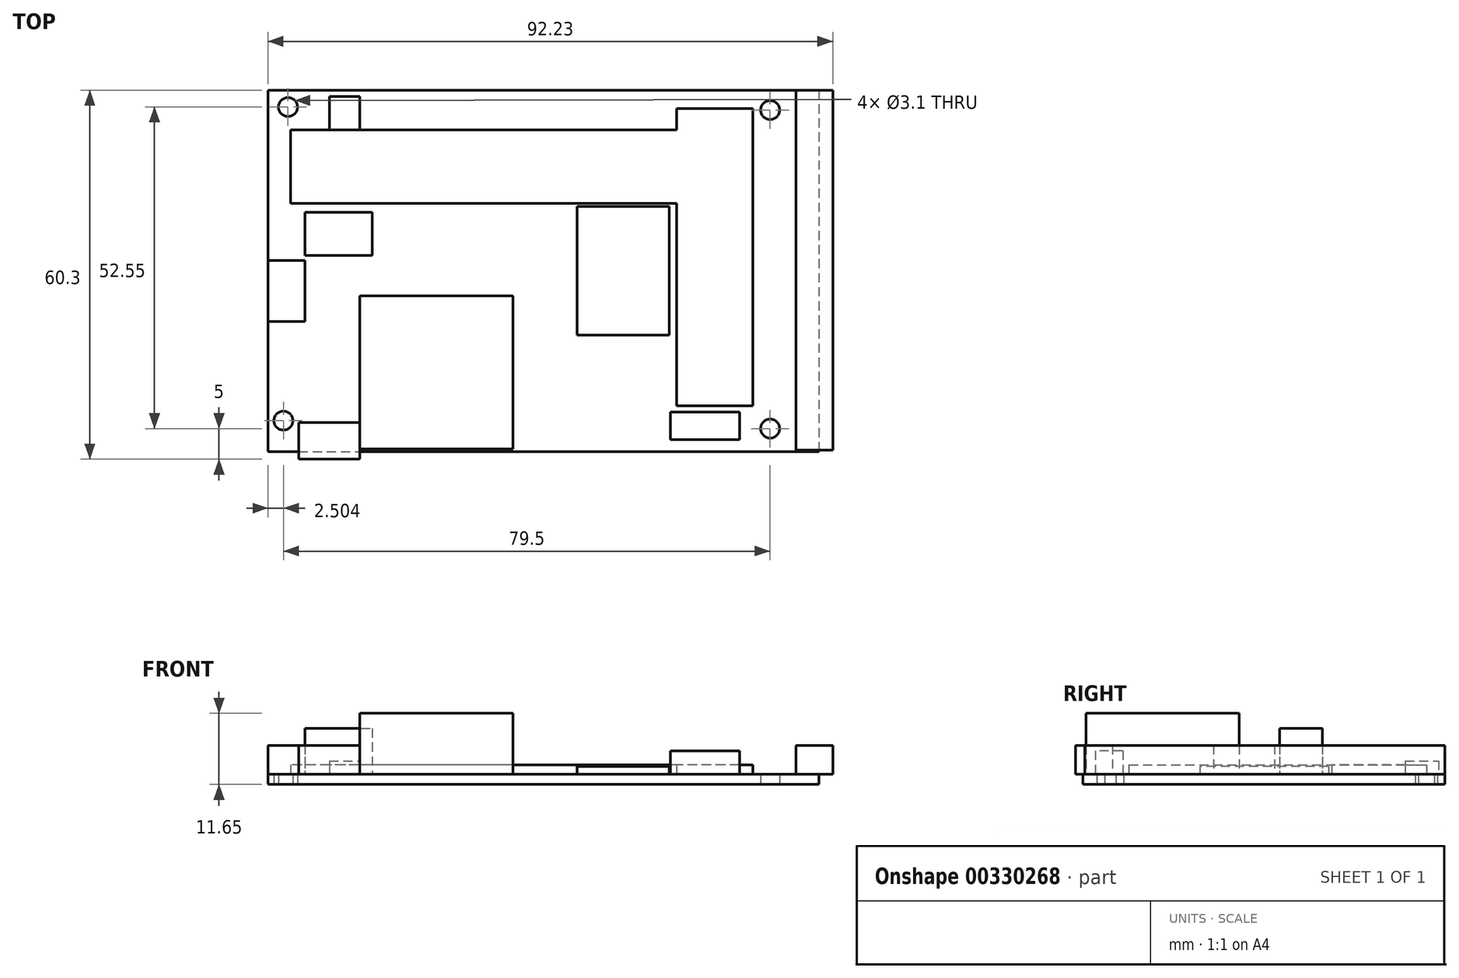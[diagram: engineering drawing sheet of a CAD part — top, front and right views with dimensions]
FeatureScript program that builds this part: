
annotation { "Feature Type Name" : "Feature", "Feature Type Description" : "" }
export const myFeature = defineFeature(function(context is Context, id is Id, definition is map)
    precondition{}
    {
        {
            var Q0;
            Q0=qCreatedBy(makeId("Top.planeOp"),FACE);
            var sketch = newSketch(context, id + "F0", { "sketchPlane" : qUnion([Q0])});
            skLineSegment(sketch, "E0.bottom", {"start": v(-45.78, 29.32) * mm, "end": v(44.22, 29.32) * mm});
            skLineSegment(sketch, "E0.top", {"start": v(-45.78, -29.78) * mm, "end": v(44.22, -29.78) * mm});
            skLineSegment(sketch, "E0.left", {"start": v(-45.78, 29.32) * mm, "end": v(-45.78, -29.78) * mm});
            skLineSegment(sketch, "E0.right", {"start": v(44.22, 29.32) * mm, "end": v(44.22, -29.78) * mm});
            skCircle(sketch, "E1", {"center": v(-43.28, -24.68) * mm, "radius": 1.55 * mm});
            skCircle(sketch, "E2", {"center": v(-42.53, 26.57) * mm, "radius": 1.55 * mm});
            skCircle(sketch, "E3", {"center": v(36.22, 26.07) * mm, "radius": 1.55 * mm});
            skCircle(sketch, "E4", {"center": v(36.22, -25.98) * mm, "radius": 1.55 * mm});
            skSolve(sketch);
        }
        {
            var Q0;
            Q0=makeQuery(id+"F0.imprint","IMPRINT",FACE,{"disambiguationData":[TD([[makeQuery(id+"F0.imprint","IMPRINT",EDGE,{"derivedFrom":sQuery(id+"F0.wireOp",EDGE,"E0.bottom")}),-1.0]])]});
            extrude(context, id + "F1", {"entities" : qUnion([Q0]), "depth" : 1.65 * mm});
        }
        {
            var Q0;
            Q0=qCreatedBy(makeId("Top.planeOp"),FACE);
            var sketch = newSketch(context, id + "F2", { "sketchPlane" : qUnion([Q0])});
            skLineSegment(sketch, "E5.bottom", {"start": v(33.42, -22.28) * mm, "end": v(20.92, -22.28) * mm});
            skLineSegment(sketch, "E5.top", {"start": v(33.42, 26.32) * mm, "end": v(20.92, 26.32) * mm});
            skLineSegment(sketch, "E5.left", {"start": v(33.42, -22.28) * mm, "end": v(33.42, 26.32) * mm});
            skLineSegment(sketch, "E5.right", {"start": v(20.92, -22.28) * mm, "end": v(20.92, 26.32) * mm});
            skLineSegment(sketch, "E6.bottom", {"start": v(20.92, 22.82) * mm, "end": v(-42.08, 22.82) * mm});
            skLineSegment(sketch, "E6.top", {"start": v(20.92, 10.82) * mm, "end": v(-42.08, 10.82) * mm});
            skLineSegment(sketch, "E6.left", {"start": v(20.92, 22.82) * mm, "end": v(20.92, 10.82) * mm});
            skLineSegment(sketch, "E6.right", {"start": v(-42.08, 22.82) * mm, "end": v(-42.08, 10.82) * mm});
            skSolve(sketch);
        }
        {
            var Q0;
            Q0 = qSketchRegion(id + "F2", true);
            extrude(context, id + "F3", {"entities" : qUnion([Q0]), "operationType" : NewBodyOperationType.ADD, "depth" : 3.2 * mm});
        }
        {
            var Q0;
            Q0=makeQuery(id+"F1.opExtrude","CAP_FACE",FACE,{"disambiguationData":[OSD([sQuery(id+"F0.wireOp",EDGE,"E0.bottom"),sQuery(id+"F0.wireOp",EDGE,"E0.top"),sQuery(id+"F0.wireOp",EDGE,"E0.left"),sQuery(id+"F0.wireOp",EDGE,"E0.right"),sQuery(id+"F0.wireOp",EDGE,"E1"),sQuery(id+"F0.wireOp",EDGE,"E2"),sQuery(id+"F0.wireOp",EDGE,"E3"),sQuery(id+"F0.wireOp",EDGE,"E4")])],"isStart":false});
            var sketch = newSketch(context, id + "F4", { "sketchPlane" : qUnion([Q0])});
            skLineSegment(sketch, "E7.bottom", {"start": v(-35.78, 22.82) * mm, "end": v(-30.78, 22.82) * mm});
            skLineSegment(sketch, "E7.top", {"start": v(-35.78, 28.32) * mm, "end": v(-30.78, 28.32) * mm});
            skLineSegment(sketch, "E7.left", {"start": v(-35.78, 22.82) * mm, "end": v(-35.78, 28.32) * mm});
            skLineSegment(sketch, "E7.right", {"start": v(-30.78, 22.82) * mm, "end": v(-30.78, 28.32) * mm});
            skSolve(sketch);
        }
        {
            var Q0;
            Q0=makeQuery(id+"F4.imprint","IMPRINT",FACE,{"disambiguationData":[TD([[makeQuery(id+"F4.imprint","IMPRINT",EDGE,{"derivedFrom":sQuery(id+"F4.wireOp",EDGE,"E7.bottom")}),1.0]])]});
            extrude(context, id + "F5", {"entities" : qUnion([Q0]), "operationType" : NewBodyOperationType.ADD, "depth" : 2.2 * mm});
        }
        {
            var Q0;
            Q0=makeQuery(id+"F1.opExtrude","CAP_FACE",FACE,{"disambiguationData":[OSD([sQuery(id+"F0.wireOp",EDGE,"E0.bottom"),sQuery(id+"F0.wireOp",EDGE,"E0.top"),sQuery(id+"F0.wireOp",EDGE,"E0.left"),sQuery(id+"F0.wireOp",EDGE,"E0.right"),sQuery(id+"F0.wireOp",EDGE,"E1"),sQuery(id+"F0.wireOp",EDGE,"E2"),sQuery(id+"F0.wireOp",EDGE,"E3"),sQuery(id+"F0.wireOp",EDGE,"E4")])],"isStart":false});
            var sketch = newSketch(context, id + "F6", { "sketchPlane" : qUnion([Q0])});
            skLineSegment(sketch, "E8.bottom", {"start": v(40.45, -29.48) * mm, "end": v(46.45, -29.48) * mm});
            skLineSegment(sketch, "E8.top", {"start": v(40.45, 29.32) * mm, "end": v(46.45, 29.32) * mm});
            skLineSegment(sketch, "E8.left", {"start": v(40.45, -29.48) * mm, "end": v(40.45, 29.32) * mm});
            skLineSegment(sketch, "E8.right", {"start": v(46.45, -29.48) * mm, "end": v(46.45, 29.32) * mm});
            skSolve(sketch);
        }
        {
            var Q0;
            {var subQ0=sQuery(id+"F6.wireOp",EDGE,"E8.right");Q0=makeQuery(id+"F6.imprint","IMPRINT",FACE,{"disambiguationData":[TD([[makeQuery(id+"F6.imprint","IMPRINT",EDGE,{"derivedFrom":subQ0}),1.0]])]});}
            var Q1;
            {var subQ0=sQuery(id+"F6.wireOp",EDGE,"E8.left");Q1=makeQuery(id+"F6.imprint","IMPRINT",FACE,{"disambiguationData":[TD([[makeQuery(id+"F6.imprint","IMPRINT",EDGE,{"derivedFrom":subQ0}),-1.0]])]});}
            extrude(context, id + "F7", {"entities" : qUnion([Q0, Q1]), "operationType" : NewBodyOperationType.ADD, "depth" : 4.75 * mm});
        }
        {
            var Q0;
            Q0=makeQuery(id+"F1.opExtrude","CAP_FACE",FACE,{"disambiguationData":[OSD([sQuery(id+"F0.wireOp",EDGE,"E0.bottom"),sQuery(id+"F0.wireOp",EDGE,"E0.top"),sQuery(id+"F0.wireOp",EDGE,"E0.left"),sQuery(id+"F0.wireOp",EDGE,"E0.right"),sQuery(id+"F0.wireOp",EDGE,"E1"),sQuery(id+"F0.wireOp",EDGE,"E2"),sQuery(id+"F0.wireOp",EDGE,"E3"),sQuery(id+"F0.wireOp",EDGE,"E4")])],"isStart":false});
            var sketch = newSketch(context, id + "F8", { "sketchPlane" : qUnion([Q0])});
            skLineSegment(sketch, "E9.bottom", {"start": v(19.72, 10.32) * mm, "end": v(4.72, 10.32) * mm});
            skLineSegment(sketch, "E9.top", {"start": v(19.72, -10.68) * mm, "end": v(4.72, -10.68) * mm});
            skLineSegment(sketch, "E9.left", {"start": v(19.72, 10.32) * mm, "end": v(19.72, -10.68) * mm});
            skLineSegment(sketch, "E9.right", {"start": v(4.72, 10.32) * mm, "end": v(4.72, -10.68) * mm});
            skSolve(sketch);
        }
        {
            var Q0;
            Q0=makeQuery(id+"F8.imprint","IMPRINT",FACE,{"disambiguationData":[TD([[makeQuery(id+"F8.imprint","IMPRINT",EDGE,{"derivedFrom":sQuery(id+"F8.wireOp",EDGE,"E9.bottom")}),1.0]])]});
            extrude(context, id + "F9", {"entities" : qUnion([Q0]), "operationType" : NewBodyOperationType.ADD, "depth" : 1.3 * mm});
        }
        {
            var Q0;
            Q0=makeQuery(id+"F1.opExtrude","CAP_FACE",FACE,{"disambiguationData":[OSD([sQuery(id+"F0.wireOp",EDGE,"E0.bottom"),sQuery(id+"F0.wireOp",EDGE,"E0.top"),sQuery(id+"F0.wireOp",EDGE,"E0.left"),sQuery(id+"F0.wireOp",EDGE,"E0.right"),sQuery(id+"F0.wireOp",EDGE,"E1"),sQuery(id+"F0.wireOp",EDGE,"E2"),sQuery(id+"F0.wireOp",EDGE,"E3"),sQuery(id+"F0.wireOp",EDGE,"E4")])],"isStart":false});
            var sketch = newSketch(context, id + "F10", { "sketchPlane" : qUnion([Q0])});
            skLineSegment(sketch, "E10.bottom", {"start": v(31.22, -23.28) * mm, "end": v(19.92, -23.28) * mm});
            skLineSegment(sketch, "E10.top", {"start": v(31.22, -27.78) * mm, "end": v(19.92, -27.78) * mm});
            skLineSegment(sketch, "E10.left", {"start": v(31.22, -23.28) * mm, "end": v(31.22, -27.78) * mm});
            skLineSegment(sketch, "E10.right", {"start": v(19.92, -23.28) * mm, "end": v(19.92, -27.78) * mm});
            skSolve(sketch);
        }
        {
            var Q0;
            Q0=makeQuery(id+"F10.imprint","IMPRINT",FACE,{"disambiguationData":[TD([[makeQuery(id+"F10.imprint","IMPRINT",EDGE,{"derivedFrom":sQuery(id+"F10.wireOp",EDGE,"E10.bottom")}),1.0]])]});
            extrude(context, id + "F11", {"entities" : qUnion([Q0]), "operationType" : NewBodyOperationType.ADD, "depth" : 3.85 * mm});
        }
        {
            var Q0;
            Q0=makeQuery(id+"F1.opExtrude","CAP_FACE",FACE,{"disambiguationData":[OSD([sQuery(id+"F0.wireOp",EDGE,"E0.bottom"),sQuery(id+"F0.wireOp",EDGE,"E0.top"),sQuery(id+"F0.wireOp",EDGE,"E0.left"),sQuery(id+"F0.wireOp",EDGE,"E0.right"),sQuery(id+"F0.wireOp",EDGE,"E1"),sQuery(id+"F0.wireOp",EDGE,"E2"),sQuery(id+"F0.wireOp",EDGE,"E3"),sQuery(id+"F0.wireOp",EDGE,"E4")])],"isStart":false});
            var sketch = newSketch(context, id + "F12", { "sketchPlane" : qUnion([Q0])});
            skLineSegment(sketch, "E11.bottom", {"start": v(-39.78, 9.34) * mm, "end": v(-28.78, 9.34) * mm});
            skLineSegment(sketch, "E11.top", {"start": v(-39.78, 2.34) * mm, "end": v(-28.78, 2.34) * mm});
            skLineSegment(sketch, "E11.left", {"start": v(-39.78, 9.34) * mm, "end": v(-39.78, 2.34) * mm});
            skLineSegment(sketch, "E11.right", {"start": v(-28.78, 9.34) * mm, "end": v(-28.78, 2.34) * mm});
            skSolve(sketch);
        }
        {
            var Q0;
            Q0=makeQuery(id+"F12.imprint","IMPRINT",FACE,{"disambiguationData":[TD([[makeQuery(id+"F12.imprint","IMPRINT",EDGE,{"derivedFrom":sQuery(id+"F12.wireOp",EDGE,"E11.bottom")}),-1.0]])]});
            extrude(context, id + "F13", {"entities" : qUnion([Q0]), "operationType" : NewBodyOperationType.ADD, "depth" : 7.5 * mm});
        }
        {
            var Q0;
            Q0=makeQuery(id+"F1.opExtrude","CAP_FACE",FACE,{"disambiguationData":[OSD([sQuery(id+"F0.wireOp",EDGE,"E0.bottom"),sQuery(id+"F0.wireOp",EDGE,"E0.top"),sQuery(id+"F0.wireOp",EDGE,"E0.left"),sQuery(id+"F0.wireOp",EDGE,"E0.right"),sQuery(id+"F0.wireOp",EDGE,"E1"),sQuery(id+"F0.wireOp",EDGE,"E2"),sQuery(id+"F0.wireOp",EDGE,"E3"),sQuery(id+"F0.wireOp",EDGE,"E4")])],"isStart":false});
            var sketch = newSketch(context, id + "F14", { "sketchPlane" : qUnion([Q0])});
            skLineSegment(sketch, "E12.bottom", {"start": v(-30.78, -4.28) * mm, "end": v(-5.78, -4.28) * mm});
            skLineSegment(sketch, "E12.top", {"start": v(-30.78, -29.28) * mm, "end": v(-5.78, -29.28) * mm});
            skLineSegment(sketch, "E12.left", {"start": v(-30.78, -4.28) * mm, "end": v(-30.78, -29.28) * mm});
            skLineSegment(sketch, "E12.right", {"start": v(-5.78, -4.28) * mm, "end": v(-5.78, -29.28) * mm});
            skSolve(sketch);
        }
        {
            var Q0;
            Q0=makeQuery(id+"F14.imprint","IMPRINT",FACE,{"disambiguationData":[TD([[makeQuery(id+"F14.imprint","IMPRINT",EDGE,{"derivedFrom":sQuery(id+"F14.wireOp",EDGE,"E12.bottom")}),-1.0]])]});
            extrude(context, id + "F15", {"entities" : qUnion([Q0]), "operationType" : NewBodyOperationType.ADD, "depth" : 10 * mm});
        }
        {
            var Q0;
            Q0=makeQuery(id+"F1.opExtrude","CAP_FACE",FACE,{"disambiguationData":[OSD([sQuery(id+"F0.wireOp",EDGE,"E0.bottom"),sQuery(id+"F0.wireOp",EDGE,"E0.top"),sQuery(id+"F0.wireOp",EDGE,"E0.left"),sQuery(id+"F0.wireOp",EDGE,"E0.right"),sQuery(id+"F0.wireOp",EDGE,"E1"),sQuery(id+"F0.wireOp",EDGE,"E2"),sQuery(id+"F0.wireOp",EDGE,"E3"),sQuery(id+"F0.wireOp",EDGE,"E4")])],"isStart":false});
            var sketch = newSketch(context, id + "F16", { "sketchPlane" : qUnion([Q0])});
            skLineSegment(sketch, "E13.bottom", {"start": v(-45.78, 1.52) * mm, "end": v(-39.78, 1.52) * mm});
            skLineSegment(sketch, "E13.top", {"start": v(-45.78, -8.48) * mm, "end": v(-39.78, -8.48) * mm});
            skLineSegment(sketch, "E13.left", {"start": v(-45.78, 1.52) * mm, "end": v(-45.78, -8.48) * mm});
            skLineSegment(sketch, "E13.right", {"start": v(-39.78, 1.52) * mm, "end": v(-39.78, -8.48) * mm});
            skLineSegment(sketch, "E14.bottom", {"start": v(-40.78, -30.98) * mm, "end": v(-30.78, -30.98) * mm});
            skLineSegment(sketch, "E14.top", {"start": v(-40.78, -24.98) * mm, "end": v(-30.78, -24.98) * mm});
            skLineSegment(sketch, "E14.left", {"start": v(-40.78, -30.98) * mm, "end": v(-40.78, -24.98) * mm});
            skLineSegment(sketch, "E14.right", {"start": v(-30.78, -30.98) * mm, "end": v(-30.78, -24.98) * mm});
            skSolve(sketch);
        }
        {
            var Q0;
            Q0=makeQuery(id+"F16.imprint","IMPRINT",FACE,{"disambiguationData":[TD([[makeQuery(id+"F16.imprint","IMPRINT",EDGE,{"derivedFrom":sQuery(id+"F16.wireOp",EDGE,"E13.bottom")}),-1.0]])]});
            var Q1;
            {var subQ2=sQuery(id+"F16.wireOp",EDGE,"E14.top");Q1=makeQuery(id+"F16.imprint","IMPRINT",FACE,{"disambiguationData":[TD([[makeQuery(id+"F16.imprint","IMPRINT",EDGE,{"derivedFrom":subQ2}),-1.0]])]});}
            var Q2;
            {var subQ0=sQuery(id+"F16.wireOp",EDGE,"E14.bottom");Q2=makeQuery(id+"F16.imprint","IMPRINT",FACE,{"disambiguationData":[TD([[makeQuery(id+"F16.imprint","IMPRINT",EDGE,{"derivedFrom":subQ0}),1.0]])]});}
            extrude(context, id + "F17", {"entities" : qUnion([Q0, Q1, Q2]), "operationType" : NewBodyOperationType.ADD, "depth" : 4.75 * mm});
        }
    });
